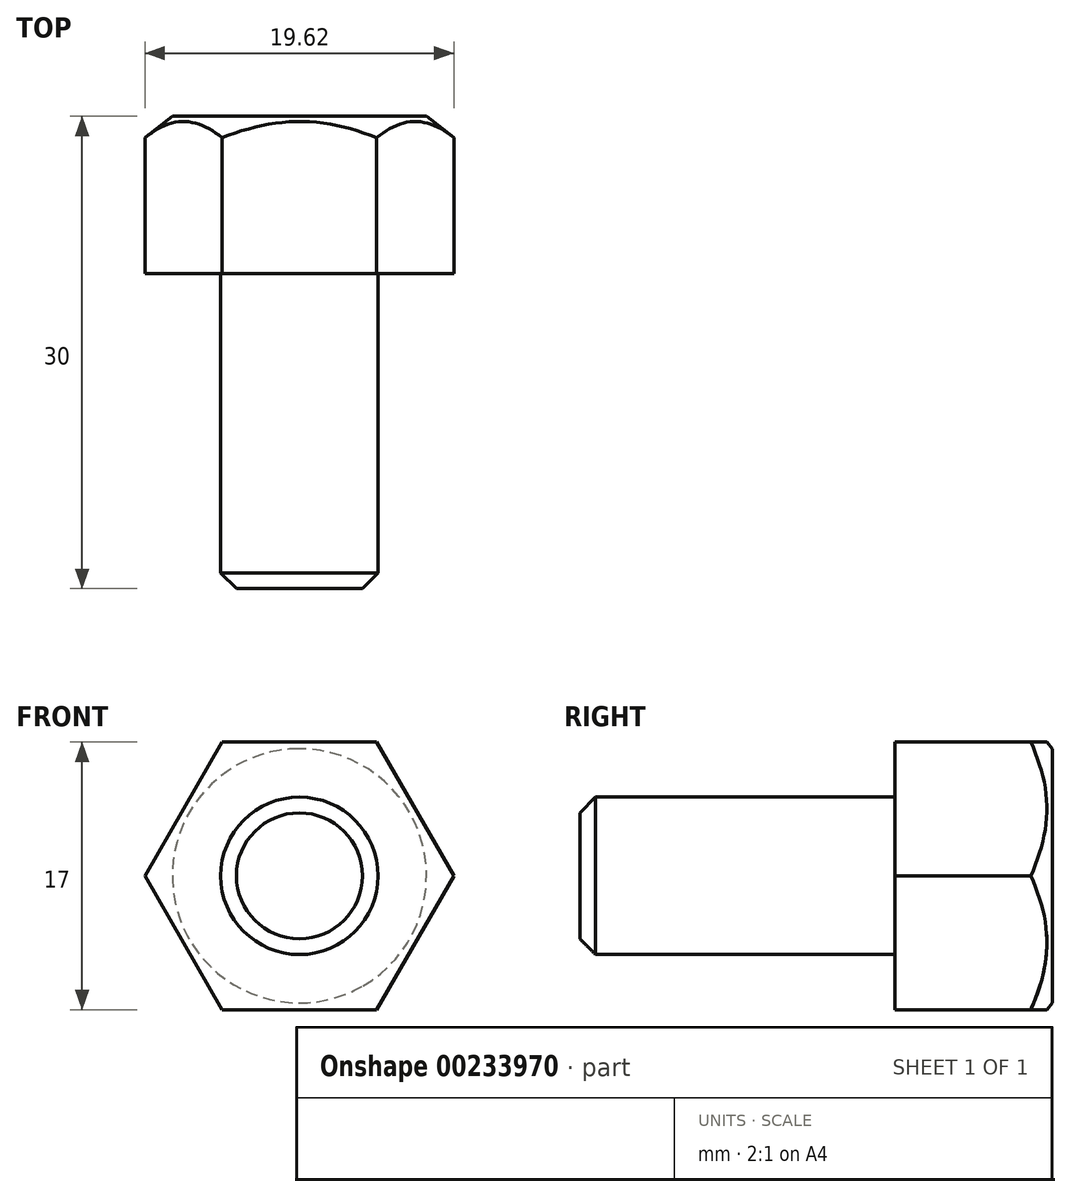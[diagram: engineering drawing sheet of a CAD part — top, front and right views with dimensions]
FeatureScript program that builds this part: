
annotation { "Feature Type Name" : "Feature", "Feature Type Description" : "" }
export const myFeature = defineFeature(function(context is Context, id is Id, definition is map)
    precondition{}
    {
        {
            assignVariable(context, id + "F0", {"name" : "L", "anyValue" : 20});
        }
        {
            var Q0;
            Q0=qCreatedBy(makeId("Front.planeOp"),FACE);
            var sketch = newSketch(context, id + "F1", { "sketchPlane" : qUnion([Q0])});
            skCircle(sketch, "E0", {"center": v(0, 0) * mm, "radius": 5 * mm});
            skSolve(sketch);
        }
        {
            var Q0;
            Q0=makeQuery(id+"F1.imprint","IMPRINT",FACE,{"disambiguationData":[TD([[makeQuery(id+"F1.imprint","IMPRINT",EDGE,{"derivedFrom":sQuery(id+"F1.wireOp",EDGE,"E0")}),1.0]])]});
            extrude(context, id + "F2", {"entities" : qUnion([Q0]), "depth" : (getVariable(context, 'L')) * mm});
        }
        {
            var Q0;
            Q0=makeQuery(id+"F2.opExtrude","CAP_FACE",FACE,{"disambiguationData":[OSD([sQuery(id+"F1.wireOp",EDGE,"E0")])],"isStart":true});
            var sketch = newSketch(context, id + "F3", { "sketchPlane" : qUnion([Q0])});
            skCircle(sketch, "E1.cCircle", {"center": v(0, 0) * mm, "radius": 8.5 * mm, "construction": true});
            skLineSegment(sketch, "E1.0", {"start": v(-4.9, 8.5) * mm, "end": v(4.9, 8.5) * mm});
            skLineSegment(sketch, "E1.1", {"start": v(4.9, 8.5) * mm, "end": v(9.81, 0) * mm});
            skLineSegment(sketch, "E1.2", {"start": v(9.81, 0) * mm, "end": v(4.9, -8.5) * mm});
            skLineSegment(sketch, "E1.3", {"start": v(4.9, -8.5) * mm, "end": v(-4.9, -8.5) * mm});
            skLineSegment(sketch, "E1.4", {"start": v(-4.9, -8.5) * mm, "end": v(-9.81, 0) * mm});
            skLineSegment(sketch, "E1.5", {"start": v(-9.81, 0) * mm, "end": v(-4.9, 8.5) * mm});
            skPoint(sketch, "E1.0.midPoint", {"position": v(0, 8.5) * mm});
            skSolve(sketch);
        }
        {
            var Q0;
            Q0=makeQuery(id+"F3.imprint","IMPRINT",FACE,{"disambiguationData":[TD([[makeQuery(id+"F3.imprint","IMPRINT",EDGE,{"derivedFrom":makeQuery(id+"F2.opExtrude","CAP_EDGE",EDGE,{"disambiguationData":[OSD([sQuery(id+"F1.wireOp",EDGE,"E0")])],"isStart":true})}),-1.0]])]});
            var Q1;
            Q1=makeQuery(id+"F3.imprint","IMPRINT",FACE,{"disambiguationData":[TD([[makeQuery(id+"F3.imprint","IMPRINT",EDGE,{"derivedFrom":sQuery(id+"F3.wireOp",EDGE,"E1.0")}),-1.0]])]});
            extrude(context, id + "F4", {"entities" : qUnion([Q0, Q1]), "operationType" : NewBodyOperationType.ADD, "depth" : 10 * mm});
        }
        {
            var Q0;
            Q0=qCreatedBy(makeId("Right.planeOp"),FACE);
            var sketch = newSketch(context, id + "F5", { "sketchPlane" : qUnion([Q0])});
            skLineSegment(sketch, "E2", {"start": v(6.72, 12.27) * mm, "end": v(10, 8.07) * mm});
            skLineSegment(sketch, "E3", {"start": v(6.72, 12.27) * mm, "end": v(13.3, 17.4) * mm});
            skLineSegment(sketch, "E4", {"start": v(13.3, 17.4) * mm, "end": v(10, 8.07) * mm});
            skSolve(sketch);
        }
        {
            var Q0;
            Q0=makeQuery(id+"F5.imprint","IMPRINT",FACE,{"disambiguationData":[TD([[makeQuery(id+"F5.imprint","IMPRINT",EDGE,{"derivedFrom":sQuery(id+"F5.wireOp",EDGE,"E2")}),1.0]])]});
            var Q1;
            Q1=makeQuery(id+"F2.opExtrude","SWEPT_FACE",FACE,{"disambiguationData":[OSD([sQuery(id+"F1.wireOp",EDGE,"E0")])]});
            revolve(context, id + "F6", {"operationType" : NewBodyOperationType.REMOVE, "entities" : qUnion([Q0]), "axis" : qUnion([Q1]), "revolveType" : RevolveType.FULL, "oppositeDirection" : true});
        }
        {
            var Q0;
            Q0=makeQuery(id+"F2.opExtrude","CAP_EDGE",EDGE,{"disambiguationData":[OSD([sQuery(id+"F1.wireOp",EDGE,"E0")])],"isStart":false});
            chamfer(context, id + "F7", {"entities" : qUnion([Q0]), "width" : 1 * mm, "tangentPropagation" : true});
        }
        {
            var Q0;
            Q0=makeQuery(id+"F2.opExtrude","SWEPT_BODY",BODY,{"disambiguationData":[OSD([sQuery(id+"F1.wireOp",EDGE,"E0")])]});
            transform(context, id + "F8", {"entities" : qUnion([Q0]), "transformType" : TransformType.TRANSLATION_3D, "dx" : 25 * mm, "dy" : 0 * mm, "dz" : 0 * mm, "makeCopy" : true});
        }
        {
            var Q0;
            Q0=makeQuery(id+"F8.opPattern","COPY",BODY,{"derivedFrom":makeQuery(id+"F2.opExtrude","SWEPT_BODY",BODY,{"disambiguationData":[OSD([sQuery(id+"F1.wireOp",EDGE,"E0")])]}),"instanceName":"1"});
            deleteBodies(context, id + "F9", {"entities" : qUnion([Q0])});
        }
        {
            var Q0;
            Q0=makeQuery(id+"F2.opExtrude","SWEPT_BODY",BODY,{"disambiguationData":[OSD([sQuery(id+"F1.wireOp",EDGE,"E0")])]});
            transform(context, id + "F10", {"entities" : qUnion([Q0]), "transformType" : TransformType.TRANSLATION_3D, "dx" : 0 * mm, "dy" : 0 * mm, "dz" : 0 * mm, "makeCopy" : true});
        }
        {
            var Q0;
            Q0=makeQuery(id+"F10.opPattern","COPY",BODY,{"derivedFrom":makeQuery(id+"F2.opExtrude","SWEPT_BODY",BODY,{"disambiguationData":[OSD([sQuery(id+"F1.wireOp",EDGE,"E0")])]}),"instanceName":"1"});
            deleteBodies(context, id + "F11", {"entities" : qUnion([Q0])});
        }
        {
            var Q0;
            Q0=makeQuery(id+"F2.opExtrude","SWEPT_BODY",BODY,{"disambiguationData":[OSD([sQuery(id+"F1.wireOp",EDGE,"E0")])]});
            transform(context, id + "F12", {"entities" : qUnion([Q0]), "transformType" : TransformType.TRANSLATION_3D, "dx" : 50 * mm, "dy" : 0 * mm, "dz" : 0 * mm, "makeCopy" : true});
        }
        {
            var Q0;
            Q0=makeQuery(id+"F12.opPattern","COPY",BODY,{"derivedFrom":makeQuery(id+"F2.opExtrude","SWEPT_BODY",BODY,{"disambiguationData":[OSD([sQuery(id+"F1.wireOp",EDGE,"E0")])]}),"instanceName":"1"});
            deleteBodies(context, id + "F13", {"entities" : qUnion([Q0])});
        }
    });
